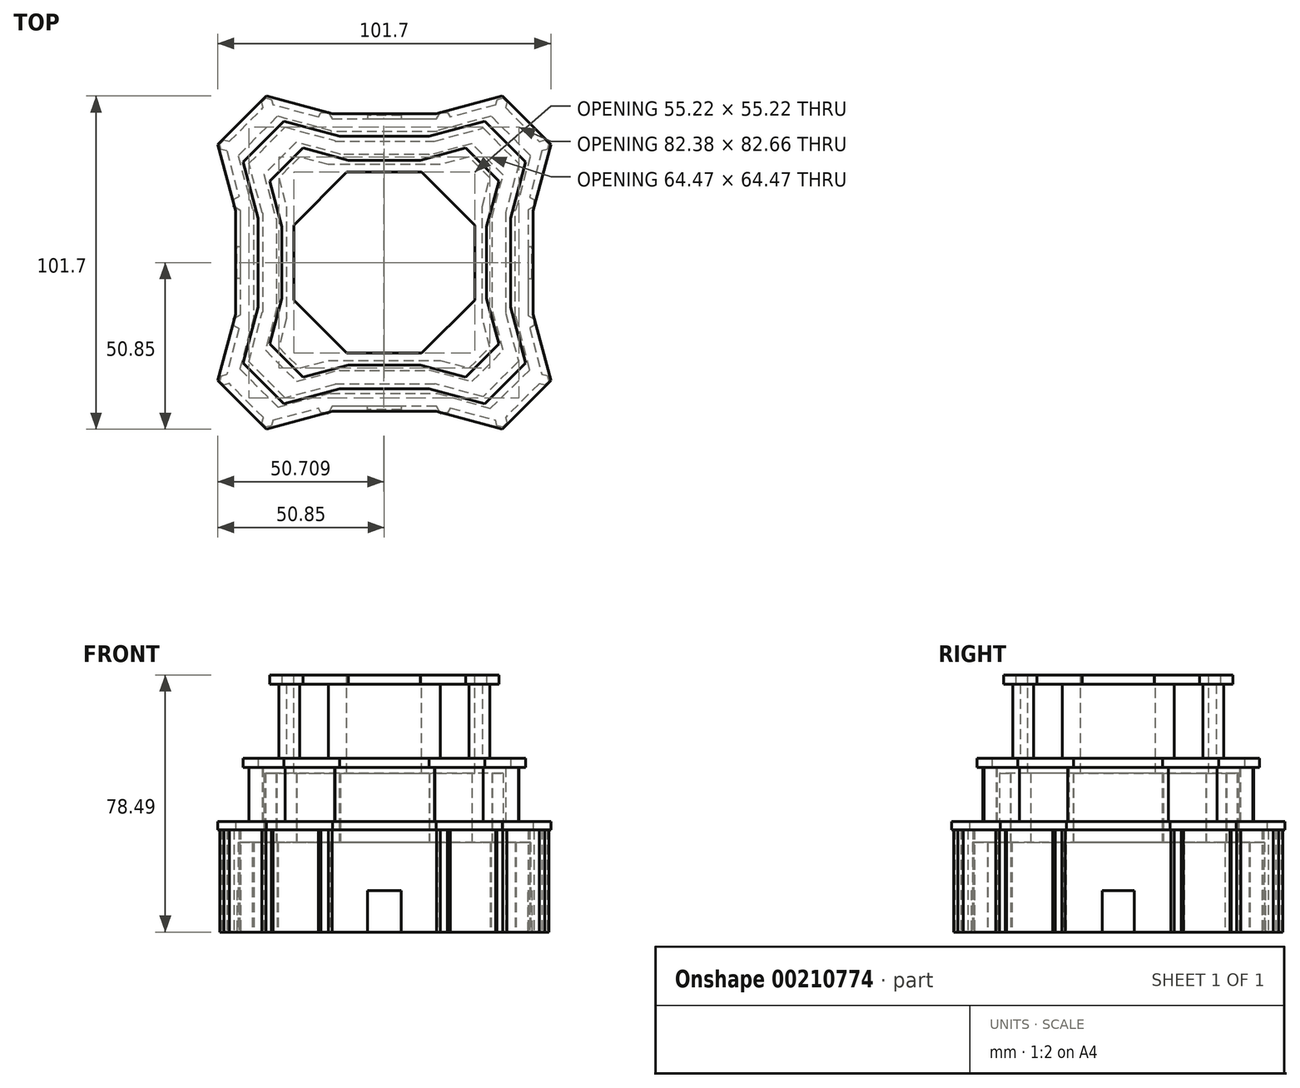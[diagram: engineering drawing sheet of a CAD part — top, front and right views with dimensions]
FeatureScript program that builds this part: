
annotation { "Feature Type Name" : "Feature", "Feature Type Description" : "" }
export const myFeature = defineFeature(function(context is Context, id is Id, definition is map)
    precondition{}
    {
        {
            var Q0;
            Q0=qCreatedBy(makeId("Top.planeOp"),FACE);
            var sketch = newSketch(context, id + "F0", { "sketchPlane" : qUnion([Q0])});
            skLineSegment(sketch, "E0.0", {"start": v(-18.18, 43.89) * mm, "end": v(18.18, 43.89) * mm});
            skLineSegment(sketch, "E0.2", {"start": v(43.89, 18.18) * mm, "end": v(43.89, -18.18) * mm});
            skLineSegment(sketch, "E0.4", {"start": v(18.18, -43.89) * mm, "end": v(-18.18, -43.89) * mm});
            skLineSegment(sketch, "E0.6", {"start": v(-43.89, -18.18) * mm, "end": v(-43.89, 18.18) * mm});
            skLineSegment(sketch, "E1.2", {"start": v(-35.7, -48.55) * mm, "end": v(-48.54, -35.75) * mm});
            skLineSegment(sketch, "E2.4", {"start": v(48.52, -35.73) * mm, "end": v(35.7, -48.52) * mm});
            skLineSegment(sketch, "E3.4", {"start": v(35.72, 48.54) * mm, "end": v(48.54, 35.72) * mm});
            skLineSegment(sketch, "E4.4", {"start": v(-48.55, 35.74) * mm, "end": v(-35.71, 48.55) * mm});
            skLineSegment(sketch, "E5.1", {"start": v(-43.89, 18.18) * mm, "end": v(-18.18, 43.89) * mm});
            skLineSegment(sketch, "E5.3", {"start": v(18.18, 43.89) * mm, "end": v(43.89, 18.18) * mm});
            skLineSegment(sketch, "E5.5", {"start": v(43.89, -18.18) * mm, "end": v(18.18, -43.89) * mm});
            skLineSegment(sketch, "E5.7", {"start": v(-18.18, -43.89) * mm, "end": v(-43.89, -18.18) * mm});
            skPoint(sketch, "E5.0.midPoint", {"position": v(-43.89, 0) * mm});
            skLineSegment(sketch, "E6", {"start": v(-18.18, 43.89) * mm, "end": v(-35.71, 48.55) * mm});
            skLineSegment(sketch, "E7", {"start": v(-48.55, 35.74) * mm, "end": v(-43.89, 18.18) * mm});
            skLineSegment(sketch, "E8", {"start": v(-43.89, -18.18) * mm, "end": v(-48.54, -35.75) * mm});
            skLineSegment(sketch, "E9", {"start": v(-35.7, -48.55) * mm, "end": v(-18.18, -43.89) * mm});
            skLineSegment(sketch, "E10", {"start": v(35.72, 48.54) * mm, "end": v(18.18, 43.89) * mm});
            skLineSegment(sketch, "E11", {"start": v(48.54, 35.72) * mm, "end": v(43.89, 18.18) * mm});
            skLineSegment(sketch, "E12", {"start": v(43.89, -18.18) * mm, "end": v(48.52, -35.73) * mm});
            skLineSegment(sketch, "E13", {"start": v(18.18, -43.89) * mm, "end": v(35.7, -48.52) * mm});
            skCircle(sketch, "E14.cCircle", {"center": v(-35.7, -48.55) * mm, "radius": 1.5 * mm, "construction": true});
            skLineSegment(sketch, "E14.0", {"start": v(-34.48, -49.79) * mm, "end": v(-36.16, -50.24) * mm});
            skLineSegment(sketch, "E14.1", {"start": v(-36.16, -50.24) * mm, "end": v(-37.39, -49) * mm});
            skLineSegment(sketch, "E14.2", {"start": v(-37.39, -49) * mm, "end": v(-36.94, -47.32) * mm});
            skLineSegment(sketch, "E14.3", {"start": v(-36.94, -47.32) * mm, "end": v(-35.25, -46.87) * mm});
            skLineSegment(sketch, "E14.4", {"start": v(-35.25, -46.87) * mm, "end": v(-34.02, -48.1) * mm});
            skLineSegment(sketch, "E14.5", {"start": v(-34.02, -48.1) * mm, "end": v(-34.48, -49.79) * mm});
            skCircle(sketch, "E15.cCircle", {"center": v(-48.54, -35.75) * mm, "radius": 1.46 * mm, "construction": true});
            skLineSegment(sketch, "E15.0", {"start": v(-48.98, -37.37) * mm, "end": v(-50.17, -36.18) * mm});
            skLineSegment(sketch, "E15.1", {"start": v(-50.17, -36.18) * mm, "end": v(-49.73, -34.56) * mm});
            skLineSegment(sketch, "E15.2", {"start": v(-49.73, -34.56) * mm, "end": v(-48.1, -34.12) * mm});
            skLineSegment(sketch, "E15.3", {"start": v(-48.1, -34.12) * mm, "end": v(-46.92, -35.32) * mm});
            skLineSegment(sketch, "E15.4", {"start": v(-46.92, -35.32) * mm, "end": v(-47.36, -36.94) * mm});
            skLineSegment(sketch, "E15.5", {"start": v(-47.36, -36.94) * mm, "end": v(-48.98, -37.37) * mm});
            skCircle(sketch, "E16.cCircle", {"center": v(35.7, -48.52) * mm, "radius": 1.56 * mm, "construction": true});
            skLineSegment(sketch, "E16.0", {"start": v(37.45, -48.99) * mm, "end": v(36.17, -50.26) * mm});
            skLineSegment(sketch, "E16.1", {"start": v(36.17, -50.26) * mm, "end": v(34.43, -49.8) * mm});
            skLineSegment(sketch, "E16.2", {"start": v(34.43, -49.8) * mm, "end": v(33.97, -48.05) * mm});
            skLineSegment(sketch, "E16.3", {"start": v(33.97, -48.05) * mm, "end": v(35.24, -46.78) * mm});
            skLineSegment(sketch, "E16.4", {"start": v(35.24, -46.78) * mm, "end": v(36.98, -47.25) * mm});
            skLineSegment(sketch, "E16.5", {"start": v(36.98, -47.25) * mm, "end": v(37.45, -48.99) * mm});
            skPoint(sketch, "E17.middle", {"position": v(0, 0) * mm});
            skCircle(sketch, "E18.cCircle", {"center": v(48.52, -35.73) * mm, "radius": 1.5 * mm, "construction": true});
            skLineSegment(sketch, "E18.0", {"start": v(50.19, -36.18) * mm, "end": v(48.96, -37.4) * mm});
            skLineSegment(sketch, "E18.1", {"start": v(48.96, -37.4) * mm, "end": v(47.29, -36.95) * mm});
            skLineSegment(sketch, "E18.2", {"start": v(47.29, -36.95) * mm, "end": v(46.84, -35.28) * mm});
            skLineSegment(sketch, "E18.3", {"start": v(46.84, -35.28) * mm, "end": v(48.07, -34.06) * mm});
            skLineSegment(sketch, "E18.4", {"start": v(48.07, -34.06) * mm, "end": v(49.74, -34.5) * mm});
            skLineSegment(sketch, "E18.5", {"start": v(49.74, -34.5) * mm, "end": v(50.19, -36.18) * mm});
            skCircle(sketch, "E19.cCircle", {"center": v(48.54, 35.72) * mm, "radius": 1.47 * mm, "construction": true});
            skLineSegment(sketch, "E19.0", {"start": v(48.97, 37.36) * mm, "end": v(50.17, 36.16) * mm});
            skLineSegment(sketch, "E19.1", {"start": v(50.17, 36.16) * mm, "end": v(49.74, 34.52) * mm});
            skLineSegment(sketch, "E19.2", {"start": v(49.74, 34.52) * mm, "end": v(48.1, 34.09) * mm});
            skLineSegment(sketch, "E19.3", {"start": v(48.1, 34.09) * mm, "end": v(46.9, 35.29) * mm});
            skLineSegment(sketch, "E19.4", {"start": v(46.9, 35.29) * mm, "end": v(47.34, 36.92) * mm});
            skLineSegment(sketch, "E19.5", {"start": v(47.34, 36.92) * mm, "end": v(48.97, 37.36) * mm});
            skCircle(sketch, "E20.cCircle", {"center": v(35.72, 48.54) * mm, "radius": 1.55 * mm, "construction": true});
            skLineSegment(sketch, "E20.0", {"start": v(36.18, 50.26) * mm, "end": v(37.45, 49) * mm});
            skLineSegment(sketch, "E20.1", {"start": v(37.45, 49) * mm, "end": v(36.99, 47.27) * mm});
            skLineSegment(sketch, "E20.2", {"start": v(36.99, 47.27) * mm, "end": v(35.26, 46.8) * mm});
            skLineSegment(sketch, "E20.3", {"start": v(35.26, 46.8) * mm, "end": v(34, 48.07) * mm});
            skLineSegment(sketch, "E20.4", {"start": v(34, 48.07) * mm, "end": v(34.46, 49.8) * mm});
            skLineSegment(sketch, "E20.5", {"start": v(34.46, 49.8) * mm, "end": v(36.18, 50.26) * mm});
            skCircle(sketch, "E21.cCircle", {"center": v(-35.71, 48.55) * mm, "radius": 1.52 * mm, "construction": true});
            skLineSegment(sketch, "E21.0", {"start": v(-37.4, 49) * mm, "end": v(-36.17, 50.25) * mm});
            skLineSegment(sketch, "E21.1", {"start": v(-36.17, 50.25) * mm, "end": v(-34.47, 49.8) * mm});
            skLineSegment(sketch, "E21.2", {"start": v(-34.47, 49.8) * mm, "end": v(-34.01, 48.1) * mm});
            skLineSegment(sketch, "E21.3", {"start": v(-34.01, 48.1) * mm, "end": v(-35.25, 46.86) * mm});
            skLineSegment(sketch, "E21.4", {"start": v(-35.25, 46.86) * mm, "end": v(-36.95, 47.31) * mm});
            skLineSegment(sketch, "E21.5", {"start": v(-36.95, 47.31) * mm, "end": v(-37.4, 49) * mm});
            skCircle(sketch, "E22.cCircle", {"center": v(-48.55, 35.74) * mm, "radius": 1.51 * mm, "construction": true});
            skLineSegment(sketch, "E22.0", {"start": v(-50.23, 36.2) * mm, "end": v(-49, 37.43) * mm});
            skLineSegment(sketch, "E22.1", {"start": v(-49, 37.43) * mm, "end": v(-47.31, 36.98) * mm});
            skLineSegment(sketch, "E22.2", {"start": v(-47.31, 36.98) * mm, "end": v(-46.86, 35.3) * mm});
            skLineSegment(sketch, "E22.3", {"start": v(-46.86, 35.3) * mm, "end": v(-48.1, 34.06) * mm});
            skLineSegment(sketch, "E22.4", {"start": v(-48.1, 34.06) * mm, "end": v(-49.78, 34.5) * mm});
            skLineSegment(sketch, "E22.5", {"start": v(-49.78, 34.5) * mm, "end": v(-50.23, 36.2) * mm});
            skCircle(sketch, "E23.cCircle", {"center": v(-43.89, 18.18) * mm, "radius": 2 * mm, "construction": true});
            skLineSegment(sketch, "E23.0", {"start": v(-45.88, 17.03) * mm, "end": v(-45.88, 19.33) * mm});
            skLineSegment(sketch, "E23.1", {"start": v(-45.88, 19.33) * mm, "end": v(-43.89, 20.48) * mm});
            skLineSegment(sketch, "E23.2", {"start": v(-43.89, 20.48) * mm, "end": v(-41.9, 19.33) * mm});
            skLineSegment(sketch, "E23.3", {"start": v(-41.9, 19.33) * mm, "end": v(-41.9, 17.03) * mm});
            skLineSegment(sketch, "E23.4", {"start": v(-41.9, 17.03) * mm, "end": v(-43.89, 15.88) * mm});
            skLineSegment(sketch, "E23.5", {"start": v(-43.89, 15.88) * mm, "end": v(-45.88, 17.03) * mm});
            skPoint(sketch, "E23.0.midPoint", {"position": v(-45.88, 18.18) * mm});
            skCircle(sketch, "E24.cCircle", {"center": v(-43.89, -18.18) * mm, "radius": 2 * mm, "construction": true});
            skLineSegment(sketch, "E24.0", {"start": v(-45.88, -19.33) * mm, "end": v(-45.88, -17.03) * mm});
            skLineSegment(sketch, "E24.1", {"start": v(-45.88, -17.03) * mm, "end": v(-43.89, -15.88) * mm});
            skLineSegment(sketch, "E24.2", {"start": v(-43.89, -15.88) * mm, "end": v(-41.9, -17.03) * mm});
            skLineSegment(sketch, "E24.3", {"start": v(-41.9, -17.03) * mm, "end": v(-41.9, -19.33) * mm});
            skLineSegment(sketch, "E24.4", {"start": v(-41.9, -19.33) * mm, "end": v(-43.89, -20.48) * mm});
            skLineSegment(sketch, "E24.5", {"start": v(-43.89, -20.48) * mm, "end": v(-45.88, -19.33) * mm});
            skPoint(sketch, "E24.0.midPoint", {"position": v(-45.88, -18.18) * mm});
            skCircle(sketch, "E25.cCircle", {"center": v(-18.18, -43.89) * mm, "radius": 1.96 * mm, "construction": true});
            skLineSegment(sketch, "E25.0", {"start": v(-17.05, -45.85) * mm, "end": v(-19.31, -45.85) * mm});
            skLineSegment(sketch, "E25.1", {"start": v(-19.31, -45.85) * mm, "end": v(-20.45, -43.89) * mm});
            skLineSegment(sketch, "E25.2", {"start": v(-20.45, -43.89) * mm, "end": v(-19.31, -41.92) * mm});
            skLineSegment(sketch, "E25.3", {"start": v(-19.31, -41.92) * mm, "end": v(-17.05, -41.92) * mm});
            skLineSegment(sketch, "E25.4", {"start": v(-17.05, -41.92) * mm, "end": v(-15.91, -43.89) * mm});
            skLineSegment(sketch, "E25.5", {"start": v(-15.91, -43.89) * mm, "end": v(-17.05, -45.85) * mm});
            skPoint(sketch, "E25.0.midPoint", {"position": v(-18.18, -45.85) * mm});
            skCircle(sketch, "E26.cCircle", {"center": v(18.18, -43.89) * mm, "radius": 1.96 * mm, "construction": true});
            skLineSegment(sketch, "E26.0", {"start": v(19.31, -45.85) * mm, "end": v(17.05, -45.85) * mm});
            skLineSegment(sketch, "E26.1", {"start": v(17.05, -45.85) * mm, "end": v(15.91, -43.89) * mm});
            skLineSegment(sketch, "E26.2", {"start": v(15.91, -43.89) * mm, "end": v(17.05, -41.92) * mm});
            skLineSegment(sketch, "E26.3", {"start": v(17.05, -41.92) * mm, "end": v(19.31, -41.92) * mm});
            skLineSegment(sketch, "E26.4", {"start": v(19.31, -41.92) * mm, "end": v(20.45, -43.89) * mm});
            skLineSegment(sketch, "E26.5", {"start": v(20.45, -43.89) * mm, "end": v(19.31, -45.85) * mm});
            skPoint(sketch, "E26.0.midPoint", {"position": v(18.18, -45.85) * mm});
            skCircle(sketch, "E27.cCircle", {"center": v(-18.18, 43.89) * mm, "radius": 1.96 * mm, "construction": true});
            skLineSegment(sketch, "E27.0", {"start": v(-17.05, 41.92) * mm, "end": v(-19.31, 41.92) * mm});
            skLineSegment(sketch, "E27.1", {"start": v(-19.31, 41.92) * mm, "end": v(-20.45, 43.89) * mm});
            skLineSegment(sketch, "E27.2", {"start": v(-20.45, 43.89) * mm, "end": v(-19.31, 45.85) * mm});
            skLineSegment(sketch, "E27.3", {"start": v(-19.31, 45.85) * mm, "end": v(-17.05, 45.85) * mm});
            skLineSegment(sketch, "E27.4", {"start": v(-17.05, 45.85) * mm, "end": v(-15.91, 43.89) * mm});
            skLineSegment(sketch, "E27.5", {"start": v(-15.91, 43.89) * mm, "end": v(-17.05, 41.92) * mm});
            skPoint(sketch, "E27.0.midPoint", {"position": v(-18.18, 41.92) * mm});
            skCircle(sketch, "E28.cCircle", {"center": v(18.18, 43.89) * mm, "radius": 1.96 * mm, "construction": true});
            skLineSegment(sketch, "E28.0", {"start": v(19.31, 41.92) * mm, "end": v(17.05, 41.92) * mm});
            skLineSegment(sketch, "E28.1", {"start": v(17.05, 41.92) * mm, "end": v(15.91, 43.89) * mm});
            skLineSegment(sketch, "E28.2", {"start": v(15.91, 43.89) * mm, "end": v(17.05, 45.85) * mm});
            skLineSegment(sketch, "E28.3", {"start": v(17.05, 45.85) * mm, "end": v(19.31, 45.85) * mm});
            skLineSegment(sketch, "E28.4", {"start": v(19.31, 45.85) * mm, "end": v(20.45, 43.89) * mm});
            skLineSegment(sketch, "E28.5", {"start": v(20.45, 43.89) * mm, "end": v(19.31, 41.92) * mm});
            skPoint(sketch, "E28.0.midPoint", {"position": v(18.18, 41.92) * mm});
            skCircle(sketch, "E29.cCircle", {"center": v(43.89, 18.18) * mm, "radius": 1.77 * mm, "construction": true});
            skLineSegment(sketch, "E29.0", {"start": v(45.66, 19.2) * mm, "end": v(45.66, 17.16) * mm});
            skLineSegment(sketch, "E29.1", {"start": v(45.66, 17.16) * mm, "end": v(43.89, 16.13) * mm});
            skLineSegment(sketch, "E29.2", {"start": v(43.89, 16.13) * mm, "end": v(42.12, 17.16) * mm});
            skLineSegment(sketch, "E29.3", {"start": v(42.12, 17.16) * mm, "end": v(42.12, 19.2) * mm});
            skLineSegment(sketch, "E29.4", {"start": v(42.12, 19.2) * mm, "end": v(43.89, 20.22) * mm});
            skLineSegment(sketch, "E29.5", {"start": v(43.89, 20.22) * mm, "end": v(45.66, 19.2) * mm});
            skPoint(sketch, "E29.0.midPoint", {"position": v(45.66, 18.18) * mm});
            skCircle(sketch, "E30.cCircle", {"center": v(43.89, -18.18) * mm, "radius": 1.77 * mm, "construction": true});
            skLineSegment(sketch, "E30.0", {"start": v(45.66, -17.16) * mm, "end": v(45.66, -19.2) * mm});
            skLineSegment(sketch, "E30.1", {"start": v(45.66, -19.2) * mm, "end": v(43.89, -20.22) * mm});
            skLineSegment(sketch, "E30.2", {"start": v(43.89, -20.22) * mm, "end": v(42.12, -19.2) * mm});
            skLineSegment(sketch, "E30.3", {"start": v(42.12, -19.2) * mm, "end": v(42.12, -17.16) * mm});
            skLineSegment(sketch, "E30.4", {"start": v(42.12, -17.16) * mm, "end": v(43.89, -16.13) * mm});
            skLineSegment(sketch, "E30.5", {"start": v(43.89, -16.13) * mm, "end": v(45.66, -17.16) * mm});
            skPoint(sketch, "E30.0.midPoint", {"position": v(45.66, -18.18) * mm});
            skLineSegment(sketch, "E31.bottom", {"start": v(28.96, 24.49) * mm, "end": v(-24.4, 24.49) * mm});
            skLineSegment(sketch, "E31.top", {"start": v(28.96, -26.25) * mm, "end": v(-24.4, -26.25) * mm});
            skLineSegment(sketch, "E31.left", {"start": v(28.96, 24.49) * mm, "end": v(28.96, -26.25) * mm});
            skLineSegment(sketch, "E31.right", {"start": v(-24.4, 24.49) * mm, "end": v(-24.4, -26.25) * mm});
            skSolve(sketch);
        }
        {
            var Q0;
            Q0 = qSketchRegion(id + "F0", true);
            extrude(context, id + "F1", {"entities" : qUnion([Q0]), "depth" : 31.24 * mm});
        }
        {
            var Q0;
            Q0=qCreatedBy(makeId("Top.planeOp"),FACE);
            var sketch = newSketch(context, id + "F2", { "sketchPlane" : qUnion([Q0])});
            skLineSegment(sketch, "E32.bottom", {"start": v(5.2, -44.91) * mm, "end": v(-5.2, -44.91) * mm});
            skLineSegment(sketch, "E32.top", {"start": v(5.2, 44.91) * mm, "end": v(-5.2, 44.91) * mm});
            skPoint(sketch, "E32.middle", {"position": v(0, 0) * mm});
            skLineSegment(sketch, "E33.left", {"start": v(45, -4.92) * mm, "end": v(45, 4.92) * mm});
            skLineSegment(sketch, "E33.right", {"start": v(-45, -4.92) * mm, "end": v(-45, 4.92) * mm});
            skLineSegment(sketch, "E34", {"start": v(-42.6, 4.92) * mm, "end": v(-42.6, -4.92) * mm});
            skLineSegment(sketch, "E35", {"start": v(-5.2, -42.68) * mm, "end": v(5.2, -42.68) * mm});
            skLineSegment(sketch, "E36", {"start": v(-5.2, 42.38) * mm, "end": v(5.2, 42.38) * mm});
            skLineSegment(sketch, "E37", {"start": v(41.75, 4.92) * mm, "end": v(41.75, -4.92) * mm});
            skLineSegment(sketch, "E38", {"start": v(5.2, 44.91) * mm, "end": v(5.2, 42.38) * mm});
            skLineSegment(sketch, "E39", {"start": v(-5.2, 44.91) * mm, "end": v(-5.2, 42.38) * mm});
            skLineSegment(sketch, "E40", {"start": v(-45, 4.92) * mm, "end": v(-42.6, 4.92) * mm});
            skLineSegment(sketch, "E41", {"start": v(-42.6, -4.92) * mm, "end": v(-45, -4.92) * mm});
            skLineSegment(sketch, "E42", {"start": v(-5.2, -44.91) * mm, "end": v(-5.2, -42.68) * mm});
            skLineSegment(sketch, "E43", {"start": v(5.2, -42.68) * mm, "end": v(5.2, -44.91) * mm});
            skLineSegment(sketch, "E44", {"start": v(41.75, 4.92) * mm, "end": v(45, 4.92) * mm});
            skLineSegment(sketch, "E45", {"start": v(41.75, -4.92) * mm, "end": v(45, -4.92) * mm});
            skSolve(sketch);
        }
        {
            var Q0;
            Q0 = qSketchRegion(id + "F2", true);
            extrude(context, id + "F3", {"entities" : qUnion([Q0]), "operationType" : NewBodyOperationType.ADD, "depth" : 12.7 * mm});
        }
        {
            var Q0;
            Q0=qCreatedBy(makeId("Top.planeOp"),FACE);
            cPlane(context, id + "F4", {"entities" : qUnion([Q0]), "cplaneType" : CPlaneType.OFFSET, "offset" : 31.24 * mm, "width" : 152.4 * mm, "height" : 152.4 * mm});
        }
        {
            var Q0;
            Q0=qCreatedBy(id+"F4.planeOp",FACE);
            var sketch = newSketch(context, id + "F5", { "sketchPlane" : qUnion([Q0])});
            skPoint(sketch, "E46.0.midPoint", {"position": v(-43.31, 0) * mm});
            skCircle(sketch, "E47.cCircle", {"center": v(-30.63, -30.63) * mm, "radius": 18.13 * mm, "construction": true});
            skLineSegment(sketch, "E47.0", {"start": v(-36.04, -50.85) * mm, "end": v(-50.85, -36.04) * mm});
            skLineSegment(sketch, "E47.1", {"start": v(-50.85, -36.04) * mm, "end": v(-45.43, -15.82) * mm});
            skLineSegment(sketch, "E47.2", {"start": v(-45.43, -15.82) * mm, "end": v(-25.2, -10.4) * mm});
            skLineSegment(sketch, "E47.3", {"start": v(-25.2, -10.4) * mm, "end": v(-10.4, -25.2) * mm});
            skLineSegment(sketch, "E47.4", {"start": v(-10.4, -25.2) * mm, "end": v(-15.82, -45.43) * mm});
            skLineSegment(sketch, "E47.5", {"start": v(-15.82, -45.43) * mm, "end": v(-36.04, -50.85) * mm});
            skPoint(sketch, "E47.0.midPoint", {"position": v(-43.45, -43.45) * mm});
            skCircle(sketch, "E48.cCircle", {"center": v(-30.63, 30.63) * mm, "radius": 18.13 * mm, "construction": true});
            skLineSegment(sketch, "E48.0", {"start": v(-50.85, 36.04) * mm, "end": v(-36.04, 50.85) * mm});
            skLineSegment(sketch, "E48.1", {"start": v(-36.04, 50.85) * mm, "end": v(-15.82, 45.43) * mm});
            skLineSegment(sketch, "E48.2", {"start": v(-15.82, 45.43) * mm, "end": v(-10.4, 25.2) * mm});
            skLineSegment(sketch, "E48.3", {"start": v(-10.4, 25.2) * mm, "end": v(-25.2, 10.4) * mm});
            skLineSegment(sketch, "E48.4", {"start": v(-25.2, 10.4) * mm, "end": v(-45.43, 15.82) * mm});
            skLineSegment(sketch, "E48.5", {"start": v(-45.43, 15.82) * mm, "end": v(-50.85, 36.04) * mm});
            skPoint(sketch, "E48.0.midPoint", {"position": v(-43.45, 43.45) * mm});
            skLineSegment(sketch, "E49.0", {"start": v(-25.18, 10.43) * mm, "end": v(-10.43, 25.18) * mm});
            skLineSegment(sketch, "E49.2", {"start": v(10.43, 25.18) * mm, "end": v(25.18, 10.43) * mm});
            skLineSegment(sketch, "E49.4", {"start": v(25.18, -10.43) * mm, "end": v(10.43, -25.18) * mm});
            skLineSegment(sketch, "E49.6", {"start": v(-10.43, -25.18) * mm, "end": v(-25.18, -10.43) * mm});
            skPoint(sketch, "E49.0.midPoint", {"position": v(-17.8, 17.8) * mm});
            skCircle(sketch, "E50.cCircle", {"center": v(30.63, 30.63) * mm, "radius": 18.13 * mm, "construction": true});
            skLineSegment(sketch, "E50.0", {"start": v(25.2, 10.4) * mm, "end": v(10.4, 25.2) * mm});
            skLineSegment(sketch, "E50.1", {"start": v(10.4, 25.2) * mm, "end": v(15.82, 45.43) * mm});
            skLineSegment(sketch, "E50.2", {"start": v(15.82, 45.43) * mm, "end": v(36.04, 50.85) * mm});
            skLineSegment(sketch, "E50.3", {"start": v(36.04, 50.85) * mm, "end": v(50.85, 36.04) * mm});
            skLineSegment(sketch, "E50.4", {"start": v(50.85, 36.04) * mm, "end": v(45.43, 15.82) * mm});
            skLineSegment(sketch, "E50.5", {"start": v(45.43, 15.82) * mm, "end": v(25.2, 10.4) * mm});
            skPoint(sketch, "E50.0.midPoint", {"position": v(17.8, 17.8) * mm});
            skCircle(sketch, "E51.cCircle", {"center": v(30.63, -30.63) * mm, "radius": 18.13 * mm, "construction": true});
            skLineSegment(sketch, "E51.0", {"start": v(10.4, -25.2) * mm, "end": v(25.2, -10.4) * mm});
            skLineSegment(sketch, "E51.1", {"start": v(25.2, -10.4) * mm, "end": v(45.43, -15.82) * mm});
            skLineSegment(sketch, "E51.2", {"start": v(45.43, -15.82) * mm, "end": v(50.85, -36.04) * mm});
            skLineSegment(sketch, "E51.3", {"start": v(50.85, -36.04) * mm, "end": v(36.04, -50.85) * mm});
            skLineSegment(sketch, "E51.4", {"start": v(36.04, -50.85) * mm, "end": v(15.82, -45.43) * mm});
            skLineSegment(sketch, "E51.5", {"start": v(15.82, -45.43) * mm, "end": v(10.4, -25.2) * mm});
            skPoint(sketch, "E51.0.midPoint", {"position": v(17.8, -17.8) * mm});
            skLineSegment(sketch, "E52", {"start": v(45.43, -15.82) * mm, "end": v(45.43, 15.82) * mm});
            skLineSegment(sketch, "E53", {"start": v(15.82, 45.43) * mm, "end": v(-15.82, 45.43) * mm});
            skLineSegment(sketch, "E54", {"start": v(-45.43, 15.82) * mm, "end": v(-45.43, -15.82) * mm});
            skLineSegment(sketch, "E55", {"start": v(-15.82, -45.43) * mm, "end": v(15.82, -45.43) * mm});
            skLineSegment(sketch, "E56", {"start": v(25.2, -10.4) * mm, "end": v(25.2, 10.4) * mm});
            skLineSegment(sketch, "E57", {"start": v(10.43, 25.18) * mm, "end": v(-10.4, 25.2) * mm});
            skLineSegment(sketch, "E58", {"start": v(-25.18, 10.43) * mm, "end": v(-25.18, -10.43) * mm});
            skLineSegment(sketch, "E59", {"start": v(-10.4, -25.2) * mm, "end": v(10.43, -25.18) * mm});
            skSolve(sketch);
        }
        {
            var Q0;
            Q0 = qSketchRegion(id + "F5", true);
            extrude(context, id + "F6", {"entities" : qUnion([Q0]), "operationType" : NewBodyOperationType.ADD, "depth" : 2.54 * mm});
        }
        {
            var Q0;
            Q0=qCreatedBy(id+"F4.planeOp",FACE);
            var sketch = newSketch(context, id + "F7", { "sketchPlane" : qUnion([Q0])});
            skCircle(sketch, "E60.cCircle", {"center": v(0, 0) * mm, "radius": 37.07 * mm, "construction": true});
            skLineSegment(sketch, "E60.0", {"start": v(-15.35, 37.07) * mm, "end": v(15.35, 37.07) * mm});
            skLineSegment(sketch, "E60.1", {"start": v(15.35, 37.07) * mm, "end": v(37.07, 15.35) * mm});
            skLineSegment(sketch, "E60.2", {"start": v(37.07, 15.35) * mm, "end": v(37.07, -15.35) * mm});
            skLineSegment(sketch, "E60.3", {"start": v(37.07, -15.35) * mm, "end": v(15.35, -37.07) * mm});
            skLineSegment(sketch, "E60.4", {"start": v(15.35, -37.07) * mm, "end": v(-15.35, -37.07) * mm});
            skLineSegment(sketch, "E60.5", {"start": v(-15.35, -37.07) * mm, "end": v(-37.07, -15.35) * mm});
            skLineSegment(sketch, "E60.6", {"start": v(-37.07, -15.35) * mm, "end": v(-37.07, 15.35) * mm});
            skLineSegment(sketch, "E60.7", {"start": v(-37.07, 15.35) * mm, "end": v(-15.35, 37.07) * mm});
            skPoint(sketch, "E60.0.midPoint", {"position": v(0, 37.07) * mm});
            skCircle(sketch, "E61.cCircle", {"center": v(-26.21, 26.21) * mm, "radius": 13.56 * mm, "construction": true});
            skLineSegment(sketch, "E61.0", {"start": v(-41.33, 30.26) * mm, "end": v(-30.26, 41.33) * mm});
            skLineSegment(sketch, "E61.1", {"start": v(-30.26, 41.33) * mm, "end": v(-15.14, 37.28) * mm});
            skLineSegment(sketch, "E61.2", {"start": v(-15.14, 37.28) * mm, "end": v(-11.1, 22.16) * mm});
            skLineSegment(sketch, "E61.3", {"start": v(-11.1, 22.16) * mm, "end": v(-22.16, 11.1) * mm});
            skLineSegment(sketch, "E61.4", {"start": v(-22.16, 11.1) * mm, "end": v(-37.28, 15.14) * mm});
            skLineSegment(sketch, "E61.5", {"start": v(-37.28, 15.14) * mm, "end": v(-41.33, 30.26) * mm});
            skPoint(sketch, "E61.0.midPoint", {"position": v(-35.8, 35.8) * mm});
            skCircle(sketch, "E62.cCircle", {"center": v(26.21, 26.21) * mm, "radius": 13.3 * mm, "construction": true});
            skLineSegment(sketch, "E62.0", {"start": v(22.24, 11.37) * mm, "end": v(11.37, 22.24) * mm});
            skLineSegment(sketch, "E62.1", {"start": v(11.37, 22.24) * mm, "end": v(15.35, 37.07) * mm});
            skLineSegment(sketch, "E62.2", {"start": v(15.35, 37.07) * mm, "end": v(30.19, 41.05) * mm});
            skLineSegment(sketch, "E62.3", {"start": v(30.19, 41.05) * mm, "end": v(41.05, 30.19) * mm});
            skLineSegment(sketch, "E62.4", {"start": v(41.05, 30.19) * mm, "end": v(37.07, 15.35) * mm});
            skLineSegment(sketch, "E62.5", {"start": v(37.07, 15.35) * mm, "end": v(22.24, 11.37) * mm});
            skPoint(sketch, "E62.0.midPoint", {"position": v(16.8, 16.8) * mm});
            skCircle(sketch, "E63.cCircle", {"center": v(26.21, -26.21) * mm, "radius": 13.2 * mm, "construction": true});
            skLineSegment(sketch, "E63.0", {"start": v(40.94, -30.16) * mm, "end": v(30.16, -40.94) * mm});
            skLineSegment(sketch, "E63.1", {"start": v(30.16, -40.94) * mm, "end": v(15.43, -37) * mm});
            skLineSegment(sketch, "E63.2", {"start": v(15.43, -37) * mm, "end": v(11.48, -22.26) * mm});
            skLineSegment(sketch, "E63.3", {"start": v(11.48, -22.26) * mm, "end": v(22.26, -11.48) * mm});
            skLineSegment(sketch, "E63.4", {"start": v(22.26, -11.48) * mm, "end": v(37, -15.43) * mm});
            skLineSegment(sketch, "E63.5", {"start": v(37, -15.43) * mm, "end": v(40.94, -30.16) * mm});
            skPoint(sketch, "E63.0.midPoint", {"position": v(35.55, -35.55) * mm});
            skCircle(sketch, "E64.cCircle", {"center": v(-26.21, -26.21) * mm, "radius": 13.56 * mm, "construction": true});
            skLineSegment(sketch, "E64.0", {"start": v(-30.26, -41.33) * mm, "end": v(-41.33, -30.26) * mm});
            skLineSegment(sketch, "E64.1", {"start": v(-41.33, -30.26) * mm, "end": v(-37.28, -15.14) * mm});
            skLineSegment(sketch, "E64.2", {"start": v(-37.28, -15.14) * mm, "end": v(-22.16, -11.1) * mm});
            skLineSegment(sketch, "E64.3", {"start": v(-22.16, -11.1) * mm, "end": v(-11.1, -22.16) * mm});
            skLineSegment(sketch, "E64.4", {"start": v(-11.1, -22.16) * mm, "end": v(-15.14, -37.28) * mm});
            skLineSegment(sketch, "E64.5", {"start": v(-15.14, -37.28) * mm, "end": v(-30.26, -41.33) * mm});
            skPoint(sketch, "E64.0.midPoint", {"position": v(-35.8, -35.8) * mm});
            skLineSegment(sketch, "E65", {"start": v(-22.16, -11.1) * mm, "end": v(-22.16, 11.1) * mm});
            skLineSegment(sketch, "E66", {"start": v(-11.1, 22.16) * mm, "end": v(11.37, 22.24) * mm});
            skLineSegment(sketch, "E67", {"start": v(22.24, 11.37) * mm, "end": v(22.26, -11.48) * mm});
            skLineSegment(sketch, "E68", {"start": v(11.48, -22.26) * mm, "end": v(-11.1, -22.16) * mm});
            skSolve(sketch);
        }
        {
            var Q0;
            Q0 = qSketchRegion(id + "F7", true);
            extrude(context, id + "F8", {"entities" : qUnion([Q0]), "operationType" : NewBodyOperationType.ADD, "depth" : 19.3 * mm});
        }
        {
            var Q0;
            Q0=qCreatedBy(id+"F4.planeOp",FACE);
            cPlane(context, id + "F9", {"entities" : qUnion([Q0]), "cplaneType" : CPlaneType.OFFSET, "offset" : 19.05 * mm, "width" : 152.4 * mm, "height" : 152.4 * mm});
        }
        {
            var Q0;
            Q0=qCreatedBy(id+"F9.planeOp",FACE);
            var sketch = newSketch(context, id + "F10", { "sketchPlane" : qUnion([Q0])});
            skLineSegment(sketch, "E69.0", {"start": v(-36.88, -15.28) * mm, "end": v(-36.88, 15.28) * mm});
            skLineSegment(sketch, "E69.2", {"start": v(-15.28, 36.88) * mm, "end": v(15.28, 36.88) * mm});
            skLineSegment(sketch, "E69.4", {"start": v(36.88, 15.28) * mm, "end": v(36.88, -15.28) * mm});
            skLineSegment(sketch, "E69.6", {"start": v(15.28, -36.88) * mm, "end": v(-15.28, -36.88) * mm});
            skPoint(sketch, "E69.0.midPoint", {"position": v(-36.88, 0) * mm});
            skCircle(sketch, "E70.cCircle", {"center": v(-26.08, -26.08) * mm, "radius": 15.28 * mm, "construction": true});
            skLineSegment(sketch, "E70.0", {"start": v(-30.64, -43.12) * mm, "end": v(-43.12, -30.64) * mm});
            skLineSegment(sketch, "E70.1", {"start": v(-43.12, -30.64) * mm, "end": v(-38.55, -13.6) * mm});
            skLineSegment(sketch, "E70.3", {"start": v(-21.51, -9.04) * mm, "end": v(-9.04, -21.51) * mm});
            skLineSegment(sketch, "E70.5", {"start": v(-13.6, -38.55) * mm, "end": v(-30.64, -43.12) * mm});
            skPoint(sketch, "E70.0.midPoint", {"position": v(-36.88, -36.88) * mm});
            skCircle(sketch, "E71.cCircle", {"center": v(-26.08, 26.08) * mm, "radius": 15.28 * mm, "construction": true});
            skLineSegment(sketch, "E71.0", {"start": v(-43.12, 30.64) * mm, "end": v(-30.64, 43.12) * mm});
            skLineSegment(sketch, "E71.1", {"start": v(-30.64, 43.12) * mm, "end": v(-13.6, 38.55) * mm});
            skLineSegment(sketch, "E71.3", {"start": v(-9.04, 21.51) * mm, "end": v(-21.51, 9.04) * mm});
            skLineSegment(sketch, "E71.5", {"start": v(-38.55, 13.6) * mm, "end": v(-43.12, 30.64) * mm});
            skPoint(sketch, "E71.0.midPoint", {"position": v(-36.88, 36.88) * mm});
            skCircle(sketch, "E72.cCircle", {"center": v(26.08, 26.08) * mm, "radius": 15.28 * mm, "construction": true});
            skLineSegment(sketch, "E72.0", {"start": v(30.64, 43.12) * mm, "end": v(43.12, 30.64) * mm});
            skLineSegment(sketch, "E72.1", {"start": v(43.12, 30.64) * mm, "end": v(38.55, 13.6) * mm});
            skLineSegment(sketch, "E72.3", {"start": v(21.51, 9.04) * mm, "end": v(9.04, 21.51) * mm});
            skLineSegment(sketch, "E72.5", {"start": v(13.6, 38.55) * mm, "end": v(30.64, 43.12) * mm});
            skPoint(sketch, "E72.0.midPoint", {"position": v(36.88, 36.88) * mm});
            skCircle(sketch, "E73.cCircle", {"center": v(26.08, -26.08) * mm, "radius": 15.28 * mm, "construction": true});
            skLineSegment(sketch, "E73.0", {"start": v(43.12, -30.64) * mm, "end": v(30.64, -43.12) * mm});
            skLineSegment(sketch, "E73.1", {"start": v(30.64, -43.12) * mm, "end": v(13.6, -38.55) * mm});
            skLineSegment(sketch, "E73.3", {"start": v(9.04, -21.51) * mm, "end": v(21.51, -9.04) * mm});
            skLineSegment(sketch, "E73.5", {"start": v(38.55, -13.6) * mm, "end": v(43.12, -30.64) * mm});
            skPoint(sketch, "E73.0.midPoint", {"position": v(36.88, -36.88) * mm});
            skLineSegment(sketch, "E74", {"start": v(-13.6, -38.55) * mm, "end": v(13.6, -38.55) * mm});
            skLineSegment(sketch, "E75", {"start": v(38.55, -13.6) * mm, "end": v(38.55, 13.6) * mm});
            skLineSegment(sketch, "E76", {"start": v(13.6, 38.55) * mm, "end": v(-13.6, 38.55) * mm});
            skLineSegment(sketch, "E77", {"start": v(-38.55, -13.6) * mm, "end": v(-38.55, 13.6) * mm});
            skLineSegment(sketch, "E78", {"start": v(-21.51, -9.04) * mm, "end": v(-21.51, 9.04) * mm});
            skLineSegment(sketch, "E79", {"start": v(9.04, -21.51) * mm, "end": v(-9.04, -21.51) * mm});
            skLineSegment(sketch, "E80", {"start": v(21.51, -9.04) * mm, "end": v(21.51, 9.04) * mm});
            skLineSegment(sketch, "E81", {"start": v(9.04, 21.51) * mm, "end": v(-9.04, 21.51) * mm});
            skSolve(sketch);
        }
        {
            var Q0;
            Q0 = qSketchRegion(id + "F10", true);
            extrude(context, id + "F11", {"entities" : qUnion([Q0]), "operationType" : NewBodyOperationType.ADD, "depth" : 2.8 * mm});
        }
        {
            var Q0;
            Q0=qCreatedBy(id+"F9.planeOp",FACE);
            var sketch = newSketch(context, id + "F12", { "sketchPlane" : qUnion([Q0])});
            skPoint(sketch, "E82.0.midPoint", {"position": v(0, 33.22) * mm});
            skCircle(sketch, "E83.cCircle", {"center": v(-23.49, -23.49) * mm, "radius": 7.84 * mm, "construction": true});
            skLineSegment(sketch, "E83.0", {"start": v(-25.83, -32.23) * mm, "end": v(-32.23, -25.83) * mm});
            skLineSegment(sketch, "E83.1", {"start": v(-32.23, -25.83) * mm, "end": v(-29.89, -17.09) * mm});
            skLineSegment(sketch, "E83.2", {"start": v(-29.89, -17.09) * mm, "end": v(-21.15, -14.75) * mm});
            skLineSegment(sketch, "E83.3", {"start": v(-21.15, -14.75) * mm, "end": v(-14.75, -21.15) * mm});
            skLineSegment(sketch, "E83.4", {"start": v(-14.75, -21.15) * mm, "end": v(-17.09, -29.89) * mm});
            skLineSegment(sketch, "E83.5", {"start": v(-17.09, -29.89) * mm, "end": v(-25.83, -32.23) * mm});
            skPoint(sketch, "E83.0.midPoint", {"position": v(-29.03, -29.03) * mm});
            skCircle(sketch, "E84.cCircle", {"center": v(23.49, -23.49) * mm, "radius": 7.84 * mm, "construction": true});
            skLineSegment(sketch, "E84.0", {"start": v(32.23, -25.83) * mm, "end": v(25.83, -32.23) * mm});
            skLineSegment(sketch, "E84.1", {"start": v(25.83, -32.23) * mm, "end": v(17.09, -29.89) * mm});
            skLineSegment(sketch, "E84.2", {"start": v(17.09, -29.89) * mm, "end": v(14.75, -21.15) * mm});
            skLineSegment(sketch, "E84.3", {"start": v(14.75, -21.15) * mm, "end": v(21.15, -14.75) * mm});
            skLineSegment(sketch, "E84.4", {"start": v(21.15, -14.75) * mm, "end": v(29.89, -17.09) * mm});
            skLineSegment(sketch, "E84.5", {"start": v(29.89, -17.09) * mm, "end": v(32.23, -25.83) * mm});
            skPoint(sketch, "E84.0.midPoint", {"position": v(29.03, -29.03) * mm});
            skCircle(sketch, "E85.cCircle", {"center": v(23.49, 23.49) * mm, "radius": 7.84 * mm, "construction": true});
            skLineSegment(sketch, "E85.0", {"start": v(25.83, 32.23) * mm, "end": v(32.23, 25.83) * mm});
            skLineSegment(sketch, "E85.1", {"start": v(32.23, 25.83) * mm, "end": v(29.89, 17.09) * mm});
            skLineSegment(sketch, "E85.2", {"start": v(29.89, 17.09) * mm, "end": v(21.15, 14.75) * mm});
            skLineSegment(sketch, "E85.3", {"start": v(21.15, 14.75) * mm, "end": v(14.75, 21.15) * mm});
            skLineSegment(sketch, "E85.4", {"start": v(14.75, 21.15) * mm, "end": v(17.09, 29.89) * mm});
            skLineSegment(sketch, "E85.5", {"start": v(17.09, 29.89) * mm, "end": v(25.83, 32.23) * mm});
            skPoint(sketch, "E85.0.midPoint", {"position": v(29.03, 29.03) * mm});
            skCircle(sketch, "E86.cCircle", {"center": v(-23.49, 23.49) * mm, "radius": 7.84 * mm, "construction": true});
            skLineSegment(sketch, "E86.0", {"start": v(-32.23, 25.83) * mm, "end": v(-25.83, 32.23) * mm});
            skLineSegment(sketch, "E86.1", {"start": v(-25.83, 32.23) * mm, "end": v(-17.09, 29.89) * mm});
            skLineSegment(sketch, "E86.2", {"start": v(-17.09, 29.89) * mm, "end": v(-14.75, 21.15) * mm});
            skLineSegment(sketch, "E86.3", {"start": v(-14.75, 21.15) * mm, "end": v(-21.15, 14.75) * mm});
            skLineSegment(sketch, "E86.4", {"start": v(-21.15, 14.75) * mm, "end": v(-29.89, 17.09) * mm});
            skLineSegment(sketch, "E86.5", {"start": v(-29.89, 17.09) * mm, "end": v(-32.23, 25.83) * mm});
            skPoint(sketch, "E86.0.midPoint", {"position": v(-29.03, 29.03) * mm});
            skLineSegment(sketch, "E87", {"start": v(-21.15, -14.75) * mm, "end": v(-21.15, 14.75) * mm});
            skLineSegment(sketch, "E88", {"start": v(-14.75, 21.15) * mm, "end": v(14.75, 21.15) * mm});
            skLineSegment(sketch, "E89", {"start": v(-14.75, -21.15) * mm, "end": v(14.75, -21.15) * mm});
            skLineSegment(sketch, "E90", {"start": v(21.15, -14.75) * mm, "end": v(21.15, 14.75) * mm});
            skLineSegment(sketch, "E91", {"start": v(17.09, -29.89) * mm, "end": v(-17.09, -29.89) * mm});
            skLineSegment(sketch, "E92", {"start": v(-29.89, -17.09) * mm, "end": v(-29.89, 17.09) * mm});
            skLineSegment(sketch, "E93", {"start": v(-17.09, 29.89) * mm, "end": v(17.09, 29.89) * mm});
            skLineSegment(sketch, "E94", {"start": v(29.89, 17.09) * mm, "end": v(29.89, -17.09) * mm});
            skSolve(sketch);
        }
        {
            var Q0;
            Q0 = qSketchRegion(id + "F12", true);
            extrude(context, id + "F13", {"entities" : qUnion([Q0]), "operationType" : NewBodyOperationType.ADD, "depth" : 25.4 * mm});
        }
        {
            var Q0;
            Q0=qCreatedBy(id+"F9.planeOp",FACE);
            cPlane(context, id + "F14", {"entities" : qUnion([Q0]), "cplaneType" : CPlaneType.OFFSET, "offset" : 25.4 * mm, "width" : 152.4 * mm, "height" : 152.4 * mm});
        }
        {
            var Q0;
            Q0=qCreatedBy(id+"F14.planeOp",FACE);
            var sketch = newSketch(context, id + "F15", { "sketchPlane" : qUnion([Q0])});
            skLineSegment(sketch, "E95.0", {"start": v(-12.38, 29.9) * mm, "end": v(12.38, 29.9) * mm});
            skLineSegment(sketch, "E95.2", {"start": v(29.9, 12.38) * mm, "end": v(29.9, -12.38) * mm});
            skLineSegment(sketch, "E95.4", {"start": v(12.38, -29.9) * mm, "end": v(-12.38, -29.9) * mm});
            skLineSegment(sketch, "E95.6", {"start": v(-29.9, -12.38) * mm, "end": v(-29.9, 12.38) * mm});
            skPoint(sketch, "E95.0.midPoint", {"position": v(0, 29.9) * mm});
            skLineSegment(sketch, "E96.0", {"start": v(-34.96, 24.84) * mm, "end": v(-24.84, 34.96) * mm});
            skLineSegment(sketch, "E96.1", {"start": v(-24.84, 34.96) * mm, "end": v(-11.03, 31.25) * mm});
            skLineSegment(sketch, "E96.3", {"start": v(-7.33, 17.44) * mm, "end": v(-17.44, 7.33) * mm});
            skLineSegment(sketch, "E96.5", {"start": v(-31.25, 11.03) * mm, "end": v(-34.96, 24.84) * mm});
            skPoint(sketch, "E96.0.midPoint", {"position": v(-29.9, 29.9) * mm});
            skLineSegment(sketch, "E97.0", {"start": v(24.84, 34.96) * mm, "end": v(34.96, 24.84) * mm});
            skLineSegment(sketch, "E97.1", {"start": v(34.96, 24.84) * mm, "end": v(31.25, 11.03) * mm});
            skLineSegment(sketch, "E97.3", {"start": v(17.44, 7.33) * mm, "end": v(7.33, 17.44) * mm});
            skLineSegment(sketch, "E97.5", {"start": v(11.03, 31.25) * mm, "end": v(24.84, 34.96) * mm});
            skPoint(sketch, "E97.0.midPoint", {"position": v(29.9, 29.9) * mm});
            skLineSegment(sketch, "E98.0", {"start": v(34.96, -24.84) * mm, "end": v(24.84, -34.96) * mm});
            skLineSegment(sketch, "E98.1", {"start": v(24.84, -34.96) * mm, "end": v(11.03, -31.25) * mm});
            skLineSegment(sketch, "E98.3", {"start": v(7.33, -17.44) * mm, "end": v(17.44, -7.33) * mm});
            skLineSegment(sketch, "E98.5", {"start": v(31.25, -11.03) * mm, "end": v(34.96, -24.84) * mm});
            skPoint(sketch, "E98.0.midPoint", {"position": v(29.9, -29.9) * mm});
            skLineSegment(sketch, "E99.0", {"start": v(-24.84, -34.96) * mm, "end": v(-34.96, -24.84) * mm});
            skLineSegment(sketch, "E99.1", {"start": v(-34.96, -24.84) * mm, "end": v(-31.25, -11.03) * mm});
            skLineSegment(sketch, "E99.3", {"start": v(-17.44, -7.33) * mm, "end": v(-7.33, -17.44) * mm});
            skLineSegment(sketch, "E99.5", {"start": v(-11.03, -31.25) * mm, "end": v(-24.84, -34.96) * mm});
            skPoint(sketch, "E99.0.midPoint", {"position": v(-29.9, -29.9) * mm});
            skLineSegment(sketch, "E100", {"start": v(-11.03, -31.25) * mm, "end": v(11.03, -31.25) * mm});
            skLineSegment(sketch, "E101", {"start": v(31.25, -11.03) * mm, "end": v(31.25, 11.03) * mm});
            skLineSegment(sketch, "E102", {"start": v(-11.03, 31.25) * mm, "end": v(11.03, 31.25) * mm});
            skLineSegment(sketch, "E103", {"start": v(-31.25, 11.03) * mm, "end": v(-31.25, -11.03) * mm});
            skLineSegment(sketch, "E104", {"start": v(-17.44, -7.33) * mm, "end": v(-17.44, 7.33) * mm});
            skLineSegment(sketch, "E105", {"start": v(-7.33, -17.44) * mm, "end": v(7.33, -17.44) * mm});
            skLineSegment(sketch, "E106", {"start": v(17.44, -7.33) * mm, "end": v(17.44, 7.33) * mm});
            skLineSegment(sketch, "E107", {"start": v(7.33, 17.44) * mm, "end": v(-7.33, 17.44) * mm});
            skSolve(sketch);
        }
        {
            var Q0;
            Q0 = qSketchRegion(id + "F15", true);
            extrude(context, id + "F16", {"entities" : qUnion([Q0]), "operationType" : NewBodyOperationType.ADD, "depth" : 2.8 * mm});
        }
        {
            var Q0;
            Q0=qCreatedBy(id+"F14.planeOp",FACE);
            var sketch = newSketch(context, id + "F17", { "sketchPlane" : qUnion([Q0])});
            skCircle(sketch, "E108.cCircle", {"center": v(0, 0) * mm, "radius": 27.61 * mm, "construction": true});
            skLineSegment(sketch, "E108.0", {"start": v(-27.61, -11.44) * mm, "end": v(-27.61, 11.44) * mm});
            skLineSegment(sketch, "E108.1", {"start": v(-27.61, 11.44) * mm, "end": v(-11.44, 27.61) * mm});
            skLineSegment(sketch, "E108.2", {"start": v(-11.44, 27.61) * mm, "end": v(11.44, 27.61) * mm});
            skLineSegment(sketch, "E108.3", {"start": v(11.44, 27.61) * mm, "end": v(27.61, 11.44) * mm});
            skLineSegment(sketch, "E108.4", {"start": v(27.61, 11.44) * mm, "end": v(27.61, -11.44) * mm});
            skLineSegment(sketch, "E108.5", {"start": v(27.61, -11.44) * mm, "end": v(11.44, -27.61) * mm});
            skLineSegment(sketch, "E108.6", {"start": v(11.44, -27.61) * mm, "end": v(-11.44, -27.61) * mm});
            skLineSegment(sketch, "E108.7", {"start": v(-11.44, -27.61) * mm, "end": v(-27.61, -11.44) * mm});
            skPoint(sketch, "E108.0.midPoint", {"position": v(-27.61, 0) * mm});
            skSolve(sketch);
        }
        {
            var Q0;
            Q0 = qSketchRegion(id + "F17", true);
            extrude(context, id + "F18", {"entities" : qUnion([Q0]), "operationType" : NewBodyOperationType.REMOVE, "endBound" : BoundingType.SYMMETRIC, "oppositeDirection" : true, "depth" : 206.76 * mm});
        }
        {
            var Q0;
            Q0=qCreatedBy(makeId("Top.planeOp"),FACE);
            var sketch = newSketch(context, id + "F19", { "sketchPlane" : qUnion([Q0])});
            skLineSegment(sketch, "E109.0", {"start": v(16.54, -39.93) * mm, "end": v(-16.54, -39.93) * mm});
            skLineSegment(sketch, "E109.1", {"start": v(-16.54, -39.93) * mm, "end": v(-39.93, -16.54) * mm});
            skLineSegment(sketch, "E109.2", {"start": v(-39.93, -16.54) * mm, "end": v(-39.93, 16.54) * mm});
            skLineSegment(sketch, "E109.3", {"start": v(-39.93, 16.54) * mm, "end": v(-16.54, 39.93) * mm});
            skLineSegment(sketch, "E109.4", {"start": v(-16.54, 39.93) * mm, "end": v(16.54, 39.93) * mm});
            skLineSegment(sketch, "E109.5", {"start": v(16.54, 39.93) * mm, "end": v(39.93, 16.54) * mm});
            skLineSegment(sketch, "E109.6", {"start": v(39.93, 16.54) * mm, "end": v(39.93, -16.54) * mm});
            skLineSegment(sketch, "E109.7", {"start": v(39.93, -16.54) * mm, "end": v(16.54, -39.93) * mm});
            skPoint(sketch, "E109.0.midPoint", {"position": v(0, -39.93) * mm});
            skCircle(sketch, "E110.cCircle", {"center": v(28.23, -28.23) * mm, "radius": 14.53 * mm, "construction": true});
            skLineSegment(sketch, "E110.0", {"start": v(44.37, -32.8) * mm, "end": v(32.34, -44.5) * mm});
            skLineSegment(sketch, "E110.1", {"start": v(32.34, -44.5) * mm, "end": v(16.2, -39.92) * mm});
            skLineSegment(sketch, "E110.2", {"start": v(16.2, -39.92) * mm, "end": v(12.1, -23.66) * mm});
            skLineSegment(sketch, "E110.3", {"start": v(12.1, -23.66) * mm, "end": v(24.12, -11.97) * mm});
            skLineSegment(sketch, "E110.4", {"start": v(24.12, -11.97) * mm, "end": v(40.27, -16.54) * mm});
            skLineSegment(sketch, "E110.5", {"start": v(40.27, -16.54) * mm, "end": v(44.37, -32.8) * mm});
            skPoint(sketch, "E110.0.midPoint", {"position": v(38.36, -38.65) * mm});
            skCircle(sketch, "E111.cCircle", {"center": v(28.23, 28.23) * mm, "radius": 14.74 * mm, "construction": true});
            skLineSegment(sketch, "E111.0", {"start": v(32.64, 44.67) * mm, "end": v(44.67, 32.64) * mm});
            skLineSegment(sketch, "E111.1", {"start": v(44.67, 32.64) * mm, "end": v(40.26, 16.2) * mm});
            skLineSegment(sketch, "E111.2", {"start": v(40.26, 16.2) * mm, "end": v(23.83, 11.8) * mm});
            skLineSegment(sketch, "E111.3", {"start": v(23.83, 11.8) * mm, "end": v(11.8, 23.83) * mm});
            skLineSegment(sketch, "E111.4", {"start": v(11.8, 23.83) * mm, "end": v(16.2, 40.26) * mm});
            skLineSegment(sketch, "E111.5", {"start": v(16.2, 40.26) * mm, "end": v(32.64, 44.67) * mm});
            skPoint(sketch, "E111.0.midPoint", {"position": v(38.65, 38.65) * mm});
            skCircle(sketch, "E112.cCircle", {"center": v(-28.23, 28.23) * mm, "radius": 14.73 * mm, "construction": true});
            skLineSegment(sketch, "E112.0", {"start": v(-44.66, 32.63) * mm, "end": v(-32.63, 44.66) * mm});
            skLineSegment(sketch, "E112.1", {"start": v(-32.63, 44.66) * mm, "end": v(-16.2, 40.26) * mm});
            skLineSegment(sketch, "E112.2", {"start": v(-16.2, 40.26) * mm, "end": v(-11.8, 23.83) * mm});
            skLineSegment(sketch, "E112.3", {"start": v(-11.8, 23.83) * mm, "end": v(-23.83, 11.8) * mm});
            skLineSegment(sketch, "E112.4", {"start": v(-23.83, 11.8) * mm, "end": v(-40.26, 16.2) * mm});
            skLineSegment(sketch, "E112.5", {"start": v(-40.26, 16.2) * mm, "end": v(-44.66, 32.63) * mm});
            skPoint(sketch, "E112.0.midPoint", {"position": v(-38.65, 38.65) * mm});
            skCircle(sketch, "E113.cCircle", {"center": v(-28.23, -28.23) * mm, "radius": 14.22 * mm, "construction": true});
            skLineSegment(sketch, "E113.0", {"start": v(-32.48, -44.1) * mm, "end": v(-44.1, -32.48) * mm});
            skLineSegment(sketch, "E113.1", {"start": v(-44.1, -32.48) * mm, "end": v(-39.85, -16.62) * mm});
            skLineSegment(sketch, "E113.2", {"start": v(-39.85, -16.62) * mm, "end": v(-23.98, -12.37) * mm});
            skLineSegment(sketch, "E113.3", {"start": v(-23.98, -12.37) * mm, "end": v(-12.37, -23.98) * mm});
            skLineSegment(sketch, "E113.4", {"start": v(-12.37, -23.98) * mm, "end": v(-16.62, -39.85) * mm});
            skLineSegment(sketch, "E113.5", {"start": v(-16.62, -39.85) * mm, "end": v(-32.48, -44.1) * mm});
            skPoint(sketch, "E113.0.midPoint", {"position": v(-38.3, -38.3) * mm});
            skSolve(sketch);
        }
        {
            var Q0;
            Q0 = qSketchRegion(id + "F19", true);
            extrude(context, id + "F20", {"entities" : qUnion([Q0]), "operationType" : NewBodyOperationType.REMOVE, "endBound" : BoundingType.SYMMETRIC, "depth" : 54.86 * mm});
        }
        {
            var Q0;
            Q0=qCreatedBy(id+"F4.planeOp",FACE);
            var sketch = newSketch(context, id + "F21", { "sketchPlane" : qUnion([Q0])});
            skCircle(sketch, "E114.cCircle", {"center": v(0, 0) * mm, "radius": 32.95 * mm, "construction": true});
            skLineSegment(sketch, "E114.0", {"start": v(32.95, 13.65) * mm, "end": v(32.95, -13.65) * mm});
            skLineSegment(sketch, "E114.1", {"start": v(32.95, -13.65) * mm, "end": v(13.65, -32.95) * mm});
            skLineSegment(sketch, "E114.2", {"start": v(13.65, -32.95) * mm, "end": v(-13.65, -32.95) * mm});
            skLineSegment(sketch, "E114.3", {"start": v(-13.65, -32.95) * mm, "end": v(-32.95, -13.65) * mm});
            skLineSegment(sketch, "E114.4", {"start": v(-32.95, -13.65) * mm, "end": v(-32.95, 13.65) * mm});
            skLineSegment(sketch, "E114.5", {"start": v(-32.95, 13.65) * mm, "end": v(-13.65, 32.95) * mm});
            skLineSegment(sketch, "E114.6", {"start": v(-13.65, 32.95) * mm, "end": v(13.65, 32.95) * mm});
            skLineSegment(sketch, "E114.7", {"start": v(13.65, 32.95) * mm, "end": v(32.95, 13.65) * mm});
            skPoint(sketch, "E114.0.midPoint", {"position": v(32.95, 0) * mm});
            skCircle(sketch, "E115.cCircle", {"center": v(23.3, -23.3) * mm, "radius": 11.64 * mm, "construction": true});
            skLineSegment(sketch, "E115.0", {"start": v(36.28, -26.78) * mm, "end": v(26.78, -36.28) * mm});
            skLineSegment(sketch, "E115.1", {"start": v(26.78, -36.28) * mm, "end": v(13.8, -32.8) * mm});
            skLineSegment(sketch, "E115.2", {"start": v(13.8, -32.8) * mm, "end": v(10.32, -19.82) * mm});
            skLineSegment(sketch, "E115.3", {"start": v(10.32, -19.82) * mm, "end": v(19.82, -10.32) * mm});
            skLineSegment(sketch, "E115.4", {"start": v(19.82, -10.32) * mm, "end": v(32.8, -13.8) * mm});
            skLineSegment(sketch, "E115.5", {"start": v(32.8, -13.8) * mm, "end": v(36.28, -26.78) * mm});
            skPoint(sketch, "E115.0.midPoint", {"position": v(31.53, -31.53) * mm});
            skCircle(sketch, "E116.cCircle", {"center": v(23.3, 23.3) * mm, "radius": 11.64 * mm, "construction": true});
            skLineSegment(sketch, "E116.0", {"start": v(26.78, 36.28) * mm, "end": v(36.28, 26.78) * mm});
            skLineSegment(sketch, "E116.1", {"start": v(36.28, 26.78) * mm, "end": v(32.8, 13.8) * mm});
            skLineSegment(sketch, "E116.2", {"start": v(32.8, 13.8) * mm, "end": v(19.82, 10.32) * mm});
            skLineSegment(sketch, "E116.3", {"start": v(19.82, 10.32) * mm, "end": v(10.32, 19.82) * mm});
            skLineSegment(sketch, "E116.4", {"start": v(10.32, 19.82) * mm, "end": v(13.8, 32.8) * mm});
            skLineSegment(sketch, "E116.5", {"start": v(13.8, 32.8) * mm, "end": v(26.78, 36.28) * mm});
            skPoint(sketch, "E116.0.midPoint", {"position": v(31.53, 31.53) * mm});
            skCircle(sketch, "E117.cCircle", {"center": v(-23.3, 23.3) * mm, "radius": 12.04 * mm, "construction": true});
            skLineSegment(sketch, "E117.0", {"start": v(-36.73, 26.9) * mm, "end": v(-26.9, 36.73) * mm});
            skLineSegment(sketch, "E117.1", {"start": v(-26.9, 36.73) * mm, "end": v(-13.47, 33.13) * mm});
            skLineSegment(sketch, "E117.2", {"start": v(-13.47, 33.13) * mm, "end": v(-9.87, 19.7) * mm});
            skLineSegment(sketch, "E117.3", {"start": v(-9.87, 19.7) * mm, "end": v(-19.7, 9.87) * mm});
            skLineSegment(sketch, "E117.4", {"start": v(-19.7, 9.87) * mm, "end": v(-33.13, 13.47) * mm});
            skLineSegment(sketch, "E117.5", {"start": v(-33.13, 13.47) * mm, "end": v(-36.73, 26.9) * mm});
            skPoint(sketch, "E117.0.midPoint", {"position": v(-31.82, 31.82) * mm});
            skCircle(sketch, "E118.cCircle", {"center": v(-23.3, -23.3) * mm, "radius": 11.64 * mm, "construction": true});
            skLineSegment(sketch, "E118.0", {"start": v(-26.78, -36.28) * mm, "end": v(-36.28, -26.78) * mm});
            skLineSegment(sketch, "E118.1", {"start": v(-36.28, -26.78) * mm, "end": v(-32.8, -13.8) * mm});
            skLineSegment(sketch, "E118.2", {"start": v(-32.8, -13.8) * mm, "end": v(-19.82, -10.32) * mm});
            skLineSegment(sketch, "E118.3", {"start": v(-19.82, -10.32) * mm, "end": v(-10.32, -19.82) * mm});
            skLineSegment(sketch, "E118.4", {"start": v(-10.32, -19.82) * mm, "end": v(-13.8, -32.8) * mm});
            skLineSegment(sketch, "E118.5", {"start": v(-13.8, -32.8) * mm, "end": v(-26.78, -36.28) * mm});
            skPoint(sketch, "E118.0.midPoint", {"position": v(-31.53, -31.53) * mm});
            skSolve(sketch);
        }
        {
            var Q0;
            Q0 = qSketchRegion(id + "F21", true);
            extrude(context, id + "F22", {"entities" : qUnion([Q0]), "operationType" : NewBodyOperationType.REMOVE, "endBound" : BoundingType.SYMMETRIC, "depth" : 34.54 * mm});
        }
    });
